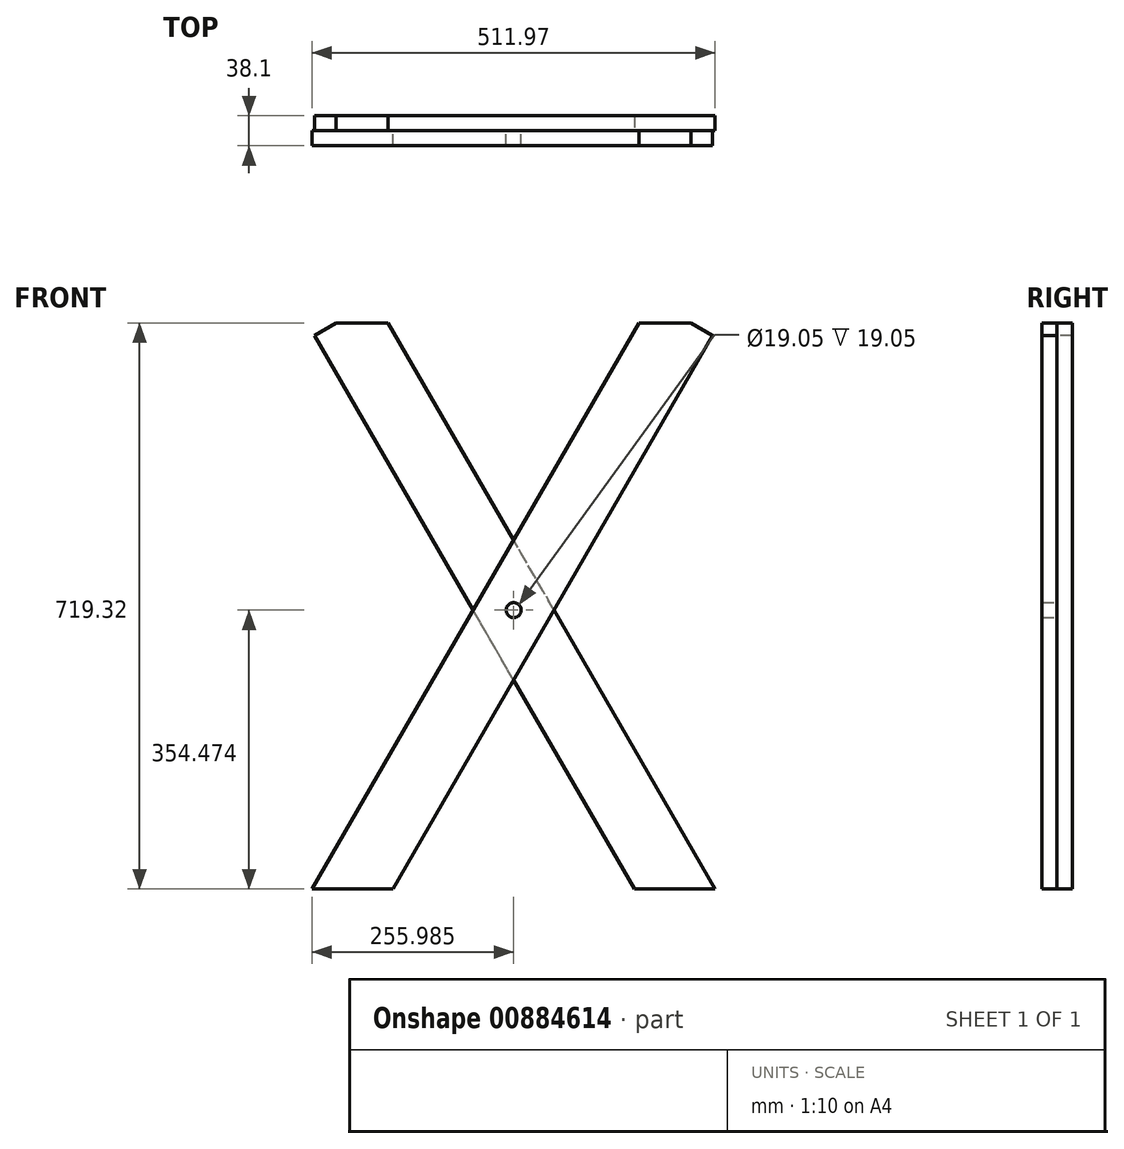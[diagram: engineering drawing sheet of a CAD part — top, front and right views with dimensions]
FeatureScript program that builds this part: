
annotation { "Feature Type Name" : "Feature", "Feature Type Description" : "" }
export const myFeature = defineFeature(function(context is Context, id is Id, definition is map)
    precondition{}
    {
        {
            var Q0;
            Q0=qCreatedBy(makeId("Front.planeOp"),FACE);
            var sketch = newSketch(context, id + "F0", { "sketchPlane" : qUnion([Q0])});
            skLineSegment(sketch, "E0", {"start": v(-238.35, 0) * mm, "end": v(176.95, 719.32) * mm});
            skLineSegment(sketch, "E1", {"start": v(-135.7, 0) * mm, "end": v(270.44, 703.45) * mm});
            skLineSegment(sketch, "E2", {"start": v(242.95, 719.32) * mm, "end": v(270.44, 703.45) * mm});
            skLineSegment(sketch, "E3", {"start": v(242.95, 719.32) * mm, "end": v(176.95, 719.32) * mm});
            skLineSegment(sketch, "E4", {"start": v(-238.35, 0) * mm, "end": v(-135.7, 0) * mm});
            skSolve(sketch);
        }
        {
            var Q0;
            Q0=makeQuery(id+"F0.imprint","IMPRINT",FACE,{"disambiguationData":[TD([[makeQuery(id+"F0.imprint","IMPRINT",EDGE,{"derivedFrom":sQuery(id+"F0.wireOp",EDGE,"E0")}),-1.0]])]});
            extrude(context, id + "F1", {"entities" : qUnion([Q0]), "depth" : 19.05 * mm, "offsetDistance" : 25.4 * mm});
        }
        {
            var Q0;
            Q0=qCreatedBy(makeId("Front.planeOp"),FACE);
            var sketch = newSketch(context, id + "F2", { "sketchPlane" : qUnion([Q0])});
            skPoint(sketch, "E5", {"position": v(17.64, 354.47) * mm});
            skSolve(sketch);
        }
        {
            var Q0;
            Q0=sQuery(id+"F2.wireOp",VERTEX,"E5");
            var Q1;
            Q1=makeQuery(id+"F1.opExtrude","SWEPT_BODY",BODY,{"disambiguationData":[OSD([sQuery(id+"F0.wireOp",EDGE,"E0"),sQuery(id+"F0.wireOp",EDGE,"E1"),sQuery(id+"F0.wireOp",EDGE,"E2"),sQuery(id+"F0.wireOp",EDGE,"E3"),sQuery(id+"F0.wireOp",EDGE,"E4")])]});
            hole(context, id + "F3", {"style" : HoleStyle.SIMPLE, "endStyle" : HoleEndStyle.THROUGH, "oppositeDirection" : true, "holeDiameter" : 19.05 * mm, "majorDiameter" : 6.35 * mm, "isTappedThrough" : true, "tappedDepth" : 12.7 * mm, "tapClearance" : 3, "locations" : qUnion([Q0]), "scope" : qUnion([Q1])});
        }
        {
            var Q0;
            Q0=qCreatedBy(makeId("Front.planeOp"),FACE);
            var sketch = newSketch(context, id + "F4", { "sketchPlane" : qUnion([Q0])});
            skLineSegment(sketch, "E6", {"start": v(273.62, 0) * mm, "end": v(-141.68, 719.32) * mm});
            skLineSegment(sketch, "E7", {"start": v(170.96, 0) * mm, "end": v(-235.17, 703.45) * mm});
            skLineSegment(sketch, "E8", {"start": v(-235.17, 703.45) * mm, "end": v(-207.68, 719.32) * mm});
            skLineSegment(sketch, "E9", {"start": v(-207.68, 719.32) * mm, "end": v(-141.68, 719.32) * mm});
            skLineSegment(sketch, "E10", {"start": v(273.62, 0) * mm, "end": v(170.96, 0) * mm});
            skSolve(sketch);
        }
        {
            var Q0;
            Q0=makeQuery(id+"F4.imprint","IMPRINT",FACE,{"disambiguationData":[TD([[makeQuery(id+"F4.imprint","IMPRINT",EDGE,{"derivedFrom":sQuery(id+"F4.wireOp",EDGE,"E6")}),1.0]])]});
            extrude(context, id + "F5", {"entities" : qUnion([Q0]), "operationType" : NewBodyOperationType.ADD, "oppositeDirection" : true, "depth" : 19.05 * mm, "offsetDistance" : 25.4 * mm});
        }
    });
